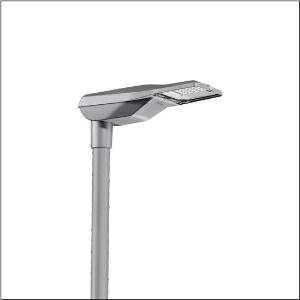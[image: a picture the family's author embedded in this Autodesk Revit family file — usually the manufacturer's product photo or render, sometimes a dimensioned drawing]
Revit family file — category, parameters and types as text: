
# Revit family: streetlight_sl_21_iq_micro___stw1_0a_5xe1e21g08cb_2b52
name_source: partatom
category: Lighting Fixtures
units: mm (PartAtom-declared; Revit-internal decimal feet)

## family parameters
Cut with Voids When Loaded = No
Host = Face
Light Source = No
Part Type = Normal
Room Calculation Point = No
Round Connector Dimension = Use Diameter
Shared = No

## types (1)
- --- (1 x LED, 2380 lm, 19.4 W, 2200K)
    Apparent Load = 19 VA
    CIE Flux Codes = 38 75 98 100 100
    Color Rendering = 70
    Color Temperature = 2200K
    Default Elevation = 1800 mm
    Description = Streetlight SL 21 iQ micro, mast luminaire, primary light control with lens, of PMMA, primary optical cover: cover, of toughened safety glass, transparent, light distribution: STW1.0a, light emission: direct distribution, primary light characteristic: asymmetric, installation type: post-top, side-entry, LED, High Power LED, rated luminous flux: 2.380lm, luminous efficacy: 123lm/W, light colour: 722, colour temperature: 2200K, control: Street-Remote, Auto-Match, Temp-Guard, Lumen-Switch, Night-Set, Smart-Wire, Light-Fading, Desk-Remote (wireless, voltage-free reading and setting of iQ features in the workshop via application-optimized NFC function/RFID function), optimised constant luminous flux control (CLO 2.0), presetting dimming linear, mains connection: 220..240V, AC, 50/60Hz, start of lifetime: 19W, end of service life: 20W, reduction: 10W, luminaire housing, of diecast aluminium, powder-coated, Siteco® metallic grey (DB 702S), corrosivity category C5 mid according to DIN EN ISO 12944, please order mast flange separately, inclination adjustable: 0°, 5°, 10°, 15°, sealing non-destructively replaceable, multi-level sealing system, length: 528mm, width: 235mm, height: 110mm, mast flange for spigot size: 42mm (side-entry): 5XC10008XM4, 60/48mm (side-entry/post-top): 5XC10108XM2, 76/60mm (side-entry/post-top): 5XC10108XM1, protection rating (complete): IP66, insulation class (complete): insulation class II (safety insulation), certification: CE, ENEC, ENEC+, VDE, impact resistance: IK09, permissible operating ambient temperature for outdoor applications: -40..+50°C, standard-compliant lighting for roads and squares, packaging unit: 1 piece

Light Distribution: STW1.0a
    Height = 110 mm
    Lamp = 1 x LED
    Lamp Light Flux = 2380 lm
    Lamp Power = 19.4 W
    Lamp count = 1
    Length = 528 mm
    Luminous efficacy = 123 lm/W
    Manufacturer = Siteco
    ModVariant = No
    Model = 5XE1E21G08CB
    Number of Poles = 1
    OnlyDefault = Yes
    Power Factor = 1
    Product Name = Streetlight SL 21 iQ micro | STW1.0a
    Product group = mast luminaire | pylon top
    ProductGroupID = 6100
    Protection Class = Protection class II
    Protection Degree = IP 66
    RLX_Detail_Level = 1
    RLX_Emergency_Light_Flux = 0 lm
    RLX_Emergency_Type = 0
    RLX_Emergency_Type_DB = No
    RlxData = <blob elided: 99005 chars, md5=9711abb2>
    Socket = socket
    Standby Power = 0 W
    System Light Flux = 2380 lm
    System Power = 19 W
    Type Comments = factory setting: luminous flux: 100 % | dim-lin: 254 | 387 mA
    Type Image = l_1006881.jpg
    URL = http://relux.com
    VarID = @adj_088301
    Voltage = 0 V
    Weight = 0.00 kg
    Width = 235 mm

## geometry (parser evidence)
native form markers: Blend x4, Sweep x9
no freeform markers — native parametric forms only
